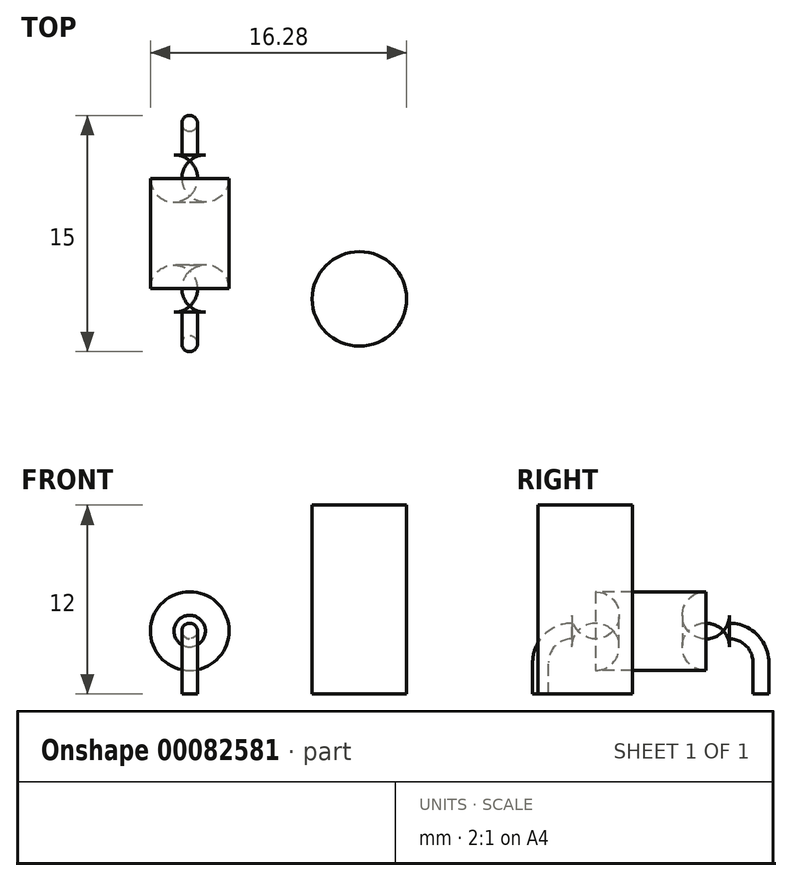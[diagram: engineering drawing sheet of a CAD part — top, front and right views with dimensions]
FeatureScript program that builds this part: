
annotation { "Feature Type Name" : "Feature", "Feature Type Description" : "" }
export const myFeature = defineFeature(function(context is Context, id is Id, definition is map)
    precondition{}
    {
        {
            var Q0;
            Q0=qCreatedBy(makeId("Top.planeOp"),FACE);
            var sketch = newSketch(context, id + "F0", { "sketchPlane" : qUnion([Q0])});
            skCircle(sketch, "E0", {"center": v(0, 0) * mm, "radius": 0.5 * mm});
            skSolve(sketch);
        }
        {
            var Q0;
            Q0=qCreatedBy(makeId("Right.planeOp"),FACE);
            var sketch = newSketch(context, id + "F1", { "sketchPlane" : qUnion([Q0])});
            skArc(sketch, "E1", {"start": v(2, 4) * mm, "mid": v(0.59, 3.41) * mm, "end": v(0, 2) * mm});
            skLineSegment(sketch, "E2", {"start": v(0, 0) * mm, "end": v(0, 2) * mm});
            skSolve(sketch);
        }
        {
            var Q0;
            Q0=qSketchRegion(id+"F0",true);
            var Q1;
            Q1=sQuery(id+"F1.wireOp",EDGE,"E1");
            var Q2;
            Q2=sQuery(id+"F1.wireOp",EDGE,"E2");
            sweep(context, id + "F2", {"profiles" : qUnion([Q0]), "path" : qUnion([Q1, Q2])});
        }
        {
            var Q0;
            Q0=makeQuery(id+"F2.opSweep","CAP_FACE",FACE,{"disambiguationData":[OSD([sQuery(id+"F0.wireOp",EDGE,"E0"),sQuery(id+"F1.wireOp",VERTEX,"E1.start")])],"isStart":false});
            var sketch = newSketch(context, id + "F3", { "sketchPlane" : qUnion([Q0])});
            skCircle(sketch, "E3.0.0", {"center": v(0, 4) * mm, "radius": 0.5 * mm});
            skCircle(sketch, "E4", {"center": v(0, 4) * mm, "radius": 2.5 * mm});
            skSolve(sketch);
        }
        {
            var Q0;
            Q0=makeQuery(id+"F3.imprint","IMPRINT",FACE,{"disambiguationData":[TD([[makeQuery(id+"F3.imprint","IMPRINT",EDGE,{"derivedFrom":sQuery(id+"F3.wireOp",EDGE,"E3.0.0")}),-1.0]])]});
            var Q1;
            Q1=makeQuery(id+"F3.imprint","IMPRINT",FACE,{"disambiguationData":[TD([[makeQuery(id+"F3.imprint","IMPRINT",EDGE,{"derivedFrom":sQuery(id+"F3.wireOp",EDGE,"E3.0.0")}),1.0]])]});
            extrude(context, id + "F4", {"entities" : qUnion([Q0, Q1]), "depth" : 10 * mm});
        }
        {
            var Q0;
            Q0=makeQuery(id+"F4.opExtrude","CAP_EDGE",EDGE,{"disambiguationData":[OSD([sQuery(id+"F3.wireOp",EDGE,"E4")])],"isStart":true});
            var Q1;
            Q1=makeQuery(id+"F4.opExtrude","CAP_EDGE",EDGE,{"disambiguationData":[OSD([sQuery(id+"F3.wireOp",EDGE,"E4")])],"isStart":false});
            fillet(context, id + "F5", {"entities" : qUnion([Q0, Q1]), "radius" : 1.5 * mm, "tangentPropagation" : true, "allowEdgeOverflow" : false});
        }
        {
            var Q0;
            Q0=makeQuery(id+"F2.opSweep","SWEPT_BODY",BODY,{"disambiguationData":[OSD([sQuery(id+"F0.wireOp",EDGE,"E0"),sQuery(id+"F1.wireOp",EDGE,"E2")])]});
            var Q1;
            Q1=makeQuery(id+"F2.opSweep","CAP_FACE",FACE,{"disambiguationData":[OSD([sQuery(id+"F0.wireOp",EDGE,"E0"),sQuery(id+"F1.wireOp",VERTEX,"E1.start")])],"isStart":false});
            mirror(context, id + "F6", {"entities" : qUnion([Q0]), "mirrorPlane" : qUnion([Q1])});
        }
        {
            var Q0;
            Q0=makeQuery(id+"F6.opPattern","COPY",BODY,{"derivedFrom":makeQuery(id+"F2.opSweep","SWEPT_BODY",BODY,{"disambiguationData":[OSD([sQuery(id+"F0.wireOp",EDGE,"E0"),sQuery(id+"F1.wireOp",EDGE,"E2")])]}),"instanceName":"1"});
            transform(context, id + "F7", {"entities" : qUnion([Q0]), "transformType" : TransformType.TRANSLATION_3D, "dx" : 0 * mm, "dy" : 10 * mm, "dz" : 0 * mm, "makeCopy" : false});
        }
        {
            var Q0;
            Q0=qCreatedBy(makeId("Top.planeOp"),FACE);
            var sketch = newSketch(context, id + "F8", { "sketchPlane" : qUnion([Q0])});
            skCircle(sketch, "E5", {"center": v(10.78, 2.85) * mm, "radius": 3 * mm});
            skSolve(sketch);
        }
        {
            var Q0;
            Q0=makeQuery(id+"F8.imprint","IMPRINT",FACE,{"disambiguationData":[TD([[makeQuery(id+"F8.imprint","IMPRINT",EDGE,{"derivedFrom":sQuery(id+"F8.wireOp",EDGE,"E5")}),1.0]])]});
            extrude(context, id + "F9", {"entities" : qUnion([Q0]), "depth" : 12 * mm});
        }
    });
